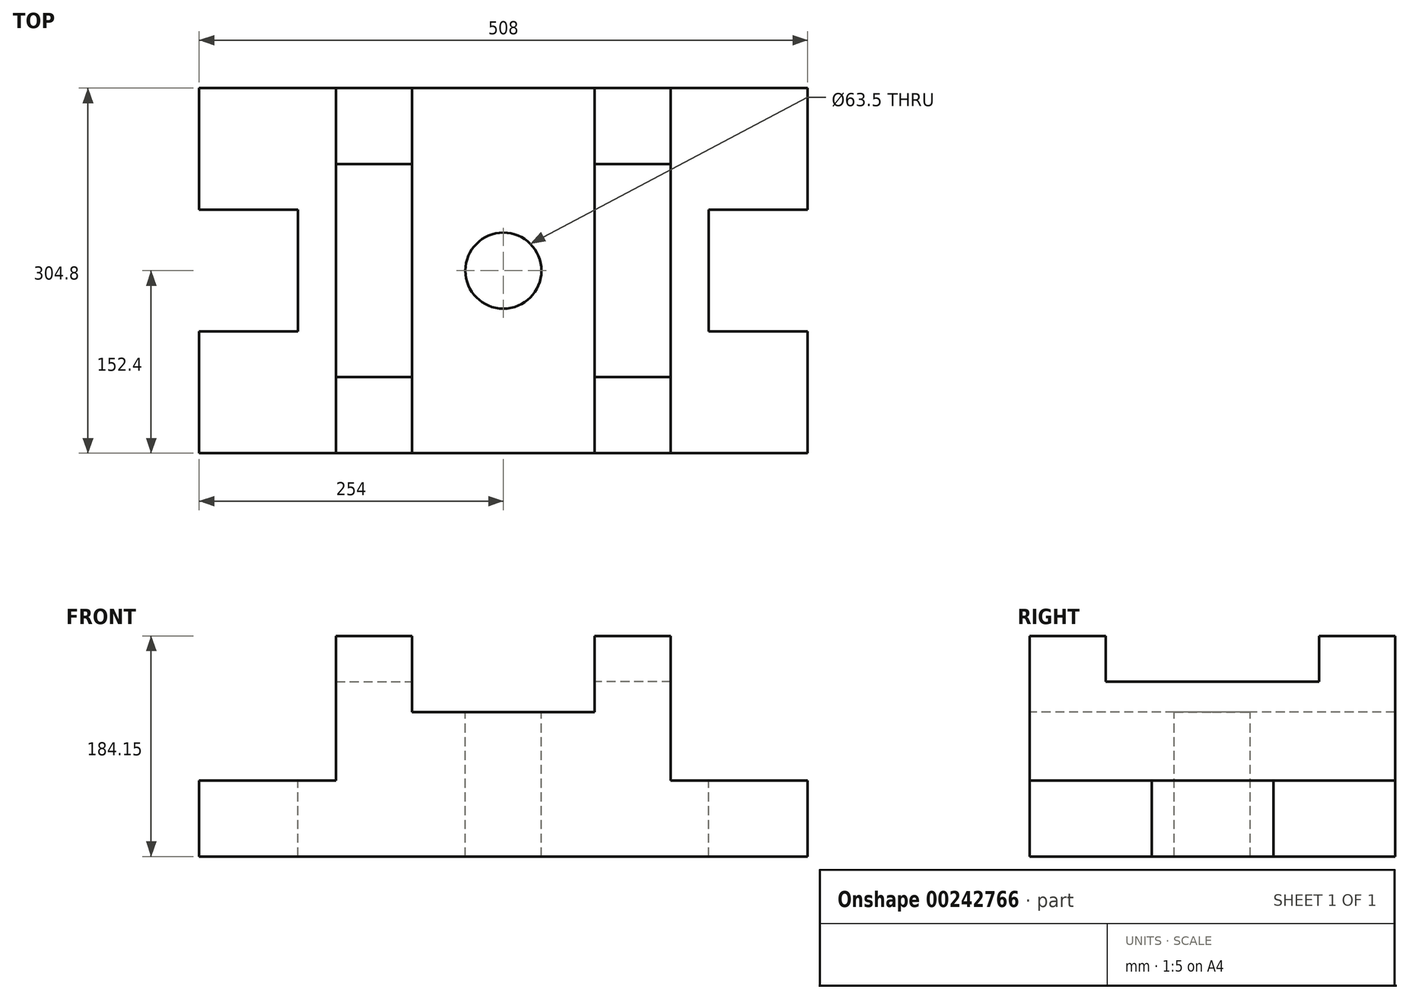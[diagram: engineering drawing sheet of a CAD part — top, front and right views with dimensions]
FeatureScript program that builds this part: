
annotation { "Feature Type Name" : "Feature", "Feature Type Description" : "" }
export const myFeature = defineFeature(function(context is Context, id is Id, definition is map)
    precondition{}
    {
        {
            var Q0;
            Q0=qCreatedBy(makeId("Top.planeOp"),FACE);
            var sketch = newSketch(context, id + "F0", { "sketchPlane" : qUnion([Q0])});
            skLineSegment(sketch, "E0.bottom", {"start": v(-127, 152.4) * mm, "end": v(381, 152.4) * mm});
            skLineSegment(sketch, "E0.top", {"start": v(-127, -152.4) * mm, "end": v(381, -152.4) * mm});
            skLineSegment(sketch, "E0.left", {"start": v(-127, 152.4) * mm, "end": v(-127, 50.8) * mm});
            skLineSegment(sketch, "E1.bottom", {"start": v(-127, 50.8) * mm, "end": v(-44.45, 50.8) * mm});
            skLineSegment(sketch, "E1.top", {"start": v(-127, -50.8) * mm, "end": v(-44.45, -50.8) * mm});
            skLineSegment(sketch, "E1.right", {"start": v(-44.45, 50.8) * mm, "end": v(-44.45, -50.8) * mm});
            skLineSegment(sketch, "E2", {"start": v(-127, 152.4) * mm, "end": v(-12.7, 152.4) * mm, "construction": true});
            skLineSegment(sketch, "E3", {"start": v(-12.7, 152.4) * mm, "end": v(-12.7, -152.4) * mm});
            skLineSegment(sketch, "E4", {"start": v(50.8, 152.4) * mm, "end": v(50.8, -152.4) * mm});
            skPoint(sketch, "E5", {"position": v(266.7, 0) * mm});
            skLineSegment(sketch, "E6.trimOffspring", {"start": v(-127, -50.8) * mm, "end": v(-127, -152.4) * mm});
            skLineSegment(sketch, "E7", {"start": v(-12.7, 88.9) * mm, "end": v(50.8, 88.9) * mm});
            skPoint(sketch, "E8.endSnap0", {"position": v(-12.7, 0) * mm});
            skLineSegment(sketch, "E9.MirrorCS", {"start": v(-12.7, -88.9) * mm, "end": v(50.8, -88.9) * mm});
            skLineSegment(sketch, "E10.MirrorCS", {"start": v(381, 50.8) * mm, "end": v(298.45, 50.8) * mm});
            skLineSegment(sketch, "E11.MirrorCS", {"start": v(381, -50.8) * mm, "end": v(381, -152.4) * mm});
            skLineSegment(sketch, "E12.MirrorCS", {"start": v(381, 152.4) * mm, "end": v(381, 50.8) * mm});
            skLineSegment(sketch, "E13.MirrorCS", {"start": v(266.7, 152.4) * mm, "end": v(266.7, -152.4) * mm});
            skLineSegment(sketch, "E14.MirrorCS", {"start": v(203.2, 152.4) * mm, "end": v(203.2, -152.4) * mm});
            skPoint(sketch, "E15", {"position": v(127, 0) * mm});
            skLineSegment(sketch, "E16.MirrorCS", {"start": v(298.45, 50.8) * mm, "end": v(298.45, -50.8) * mm});
            skLineSegment(sketch, "E17.MirrorCS", {"start": v(381, -50.8) * mm, "end": v(298.45, -50.8) * mm});
            skLineSegment(sketch, "E18.MirrorCS", {"start": v(266.7, 88.9) * mm, "end": v(203.2, 88.9) * mm});
            skLineSegment(sketch, "E19.MirrorCS", {"start": v(266.7, -88.9) * mm, "end": v(203.2, -88.9) * mm});
            skCircle(sketch, "E20", {"center": v(127, 0) * mm, "radius": 31.75 * mm});
            skLineSegment(sketch, "E21", {"start": v(127, 152.4) * mm, "end": v(127, -152.4) * mm, "construction": true});
            skLineSegment(sketch, "E22", {"start": v(368.91, 0) * mm, "end": v(-139.31, 0) * mm, "construction": true});
            skPoint(sketch, "E22.startSnap0", {"position": v(298.45, 0) * mm});
            skPoint(sketch, "E22.endSnap0", {"position": v(-44.45, 0) * mm});
            skSolve(sketch);
        }
        {
            var Q0;
            {var subQ0=sQuery(id+"F0.wireOp",EDGE,"E0.left");Q0=makeQuery(id+"F0.imprint","IMPRINT",FACE,{"disambiguationData":[TD([[makeQuery(id+"F0.imprint","IMPRINT",EDGE,{"derivedFrom":subQ0}),1.0]])]});}
            var Q1;
            {var subQ5=sQuery(id+"F0.wireOp",EDGE,"E7");Q1=makeQuery(id+"F0.imprint","IMPRINT",FACE,{"disambiguationData":[TD([[makeQuery(id+"F0.imprint","IMPRINT",EDGE,{"derivedFrom":subQ5}),1.0]])]});}
            var Q2;
            {var subQ0=sQuery(id+"F0.wireOp",EDGE,"E7");Q2=makeQuery(id+"F0.imprint","IMPRINT",FACE,{"disambiguationData":[TD([[makeQuery(id+"F0.imprint","IMPRINT",EDGE,{"derivedFrom":subQ0}),-1.0]])]});}
            var Q3;
            {var subQ5=sQuery(id+"F0.wireOp",EDGE,"E9.MirrorCS");Q3=makeQuery(id+"F0.imprint","IMPRINT",FACE,{"disambiguationData":[TD([[makeQuery(id+"F0.imprint","IMPRINT",EDGE,{"derivedFrom":subQ5}),-1.0]])]});}
            var Q4;
            {var subQ0=sQuery(id+"F0.wireOp",EDGE,"E18.MirrorCS");Q4=makeQuery(id+"F0.imprint","IMPRINT",FACE,{"disambiguationData":[TD([[makeQuery(id+"F0.imprint","IMPRINT",EDGE,{"derivedFrom":subQ0}),1.0]])]});}
            var Q5;
            {var subQ5=sQuery(id+"F0.wireOp",EDGE,"E18.MirrorCS");Q5=makeQuery(id+"F0.imprint","IMPRINT",FACE,{"disambiguationData":[TD([[makeQuery(id+"F0.imprint","IMPRINT",EDGE,{"derivedFrom":subQ5}),-1.0]])]});}
            var Q6;
            {var subQ5=sQuery(id+"F0.wireOp",EDGE,"E19.MirrorCS");Q6=makeQuery(id+"F0.imprint","IMPRINT",FACE,{"disambiguationData":[TD([[makeQuery(id+"F0.imprint","IMPRINT",EDGE,{"derivedFrom":subQ5}),1.0]])]});}
            var Q7;
            Q7=makeQuery(id+"F0.imprint","IMPRINT",FACE,{"disambiguationData":[TD([[makeQuery(id+"F0.imprint","IMPRINT",EDGE,{"derivedFrom":sQuery(id+"F0.wireOp",EDGE,"E10.MirrorCS")}),-1.0]])]});
            var Q8;
            Q8=makeQuery(id+"F0.imprint","IMPRINT",FACE,{"disambiguationData":[TD([[makeQuery(id+"F0.imprint","IMPRINT",EDGE,{"derivedFrom":sQuery(id+"F0.wireOp",EDGE,"E20")}),-1.0]])]});
            extrude(context, id + "F1", {"entities" : qUnion([Q0, Q1, Q2, Q3, Q4, Q5, Q6, Q7, Q8]), "oppositeDirection" : true, "depth" : 184.15 * mm});
        }
        {
            var Q0;
            {var subQ0=sQuery(id+"F0.wireOp",EDGE,"E0.left");Q0=makeQuery(id+"F0.imprint","IMPRINT",FACE,{"disambiguationData":[TD([[makeQuery(id+"F0.imprint","IMPRINT",EDGE,{"derivedFrom":subQ0}),1.0]])]});}
            var Q1;
            Q1=makeQuery(id+"F0.imprint","IMPRINT",FACE,{"disambiguationData":[TD([[makeQuery(id+"F0.imprint","IMPRINT",EDGE,{"derivedFrom":sQuery(id+"F0.wireOp",EDGE,"E10.MirrorCS")}),-1.0]])]});
            extrude(context, id + "F2", {"entities" : qUnion([Q0, Q1]), "operationType" : NewBodyOperationType.REMOVE, "oppositeDirection" : true, "depth" : 120.65 * mm});
        }
        {
            var Q0;
            Q0=makeQuery(id+"F0.imprint","IMPRINT",FACE,{"disambiguationData":[TD([[makeQuery(id+"F0.imprint","IMPRINT",EDGE,{"derivedFrom":sQuery(id+"F0.wireOp",EDGE,"E20")}),-1.0]])]});
            extrude(context, id + "F3", {"entities" : qUnion([Q0]), "operationType" : NewBodyOperationType.REMOVE, "oppositeDirection" : true, "depth" : 63.5 * mm});
        }
        {
            var Q0;
            {var subQ0=sQuery(id+"F0.wireOp",EDGE,"E7");Q0=makeQuery(id+"F0.imprint","IMPRINT",FACE,{"disambiguationData":[TD([[makeQuery(id+"F0.imprint","IMPRINT",EDGE,{"derivedFrom":subQ0}),-1.0]])]});}
            var Q1;
            {var subQ0=sQuery(id+"F0.wireOp",EDGE,"E18.MirrorCS");Q1=makeQuery(id+"F0.imprint","IMPRINT",FACE,{"disambiguationData":[TD([[makeQuery(id+"F0.imprint","IMPRINT",EDGE,{"derivedFrom":subQ0}),1.0]])]});}
            extrude(context, id + "F4", {"entities" : qUnion([Q0, Q1]), "operationType" : NewBodyOperationType.REMOVE, "oppositeDirection" : true, "depth" : 38.1 * mm});
        }
    });
